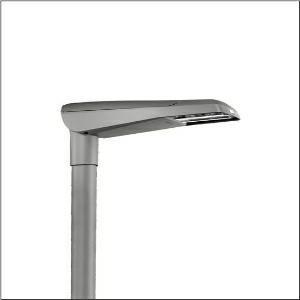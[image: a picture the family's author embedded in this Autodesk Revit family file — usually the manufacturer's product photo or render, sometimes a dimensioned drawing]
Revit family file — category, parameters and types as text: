
# Revit family: streetlight_sl_11_iq_micro___st1_0a_5xc1mc1f08de_be1f
name_source: partatom
category: Lighting Fixtures
units: mm (PartAtom-declared; Revit-internal decimal feet)

## family parameters
Cut with Voids When Loaded = No
Host = Face
Light Source = No
Part Type = Normal
Room Calculation Point = No
Round Connector Dimension = Use Diameter
Shared = No

## types (1)
- --- (1 x LED, 3740 lm, 27.4 W, 4000K)
    Apparent Load = 27 VA
    CIE Flux Codes = 33 66 96 100 100
    Color Rendering = 70
    Color Temperature = 4000K
    Default Elevation = 1800 mm
    Description = Streetlight SL 11 iQ micro, mast luminaire, primary light control with 3 zone facetted reflector, of plastic, silver coated, highly specular, primary optical cover: cover, of PMMA, transparent, light distribution: ST1.0a, light emission: direct distribution, primary light characteristic: asymmetric, installation type: post-top, side-entry, lamps: LED, High Power LED, rated values: 3.510lm | 27,7W | 126,7lm/W (begin service life); end service life: 3.510lm | 28,1W; at 50% lumin. flux: 1.755lm | 13,4W | 131lm/W, colour temperature: 2200/2700/3000/4000K, colour rendering: CRI > 70, light colour: 722/727/730/740, light setting 1 begin service life: 100% | 3.510lm | 27,7W | 126,7lm/W | 3.000K, light setting 1 end service life: 28,1W, further light settings possible, control: Street-Remote, Auto-Match, Temp-Guard, Lumen-Switch, Night-Set, Smart-Wire, Light-Fading, Desk-Remote (wireless, voltage-free reading and setting of iQ features in the workshop via application-optimized NFC function/RFID function), optimised constant luminous flux control (CLO 2.0), with cable H07RN-F 3x 1.5mm², mains connection: 220..240V, AC, 50/60Hz, connection cable pre-assembled, cable length: 6,5m, luminaire housing, of diecast aluminium, powder-coated, SITECO metallic grey (DB 702S), please order mast flange separately, inclination adjustable without tools: 0°, 5°, 10°, 15° (post-top) | 0°, -5°, -10°, -15° (side-entry), sealing non-destructively replaceable, multi-level sealing system, length: 600mm, width: 174mm, height: 116mm, mast flange for spigot size: 42mm (side-entry): 5XC10008XM4, 60/48mm (side-entry/post-top): 5XC10108XM2, 76/60mm (side-entry/post-top): 5XC10108XM1, equipment: Power, protection rating (complete): IP66, insulation class (complete): insulation class II (safety insulation), certification: CE, ENEC, ENEC+, VDE, impact resistance: IK10, permissible operating ambient temperature for outdoor applications: -25..+50°C, standard-compliant lighting for roads and squares, Environmental Product Declaration (EPD) tested and certified by an independent institute, packaging unit: 1 piece

Light Distribution: ST1.0a
    Height = 116 mm
    Lamp = 1 x LED
    Lamp Light Flux = 3740 lm
    Lamp Power = 27.4 W
    Lamp count = 1
    Length = 600 mm
    Luminous efficacy = 137 lm/W
    Manufacturer = Siteco
    ModVariant = No
    Model = 5XC1MC1F08DE
    Number of Poles = 1
    OnlyDefault = Yes
    Power Factor = 1
    Product Name = Streetlight SL 11 iQ micro | ST1.0a
    Product group = mast luminaire | pylon top
    ProductGroupID = 6100
    Protection Class = Protection class II
    Protection Degree = IP 66
    RLX_Detail_Level = 1
    RLX_Emergency_Light_Flux = 0 lm
    RLX_Emergency_Type = 0
    RLX_Emergency_Type_DB = No
    RlxData = <blob elided: 59089 chars, md5=e0ce2712>
    Socket = socket
    Standby Power = 0 W
    System Light Flux = 3740 lm
    System Power = 27 W
    Type Comments = individual setting: luminous flux: 100 % | dim-lin: 254 | 726 mA
    Type Image = l_1006566.jpg
    URL = http://relux.com
    VarID = @adj_048387
    Voltage = 0 V
    Weight = 0.00 kg
    Width = 174 mm

## geometry (parser evidence)
native form markers: Blend x4, Sweep x11
no freeform markers — native parametric forms only
